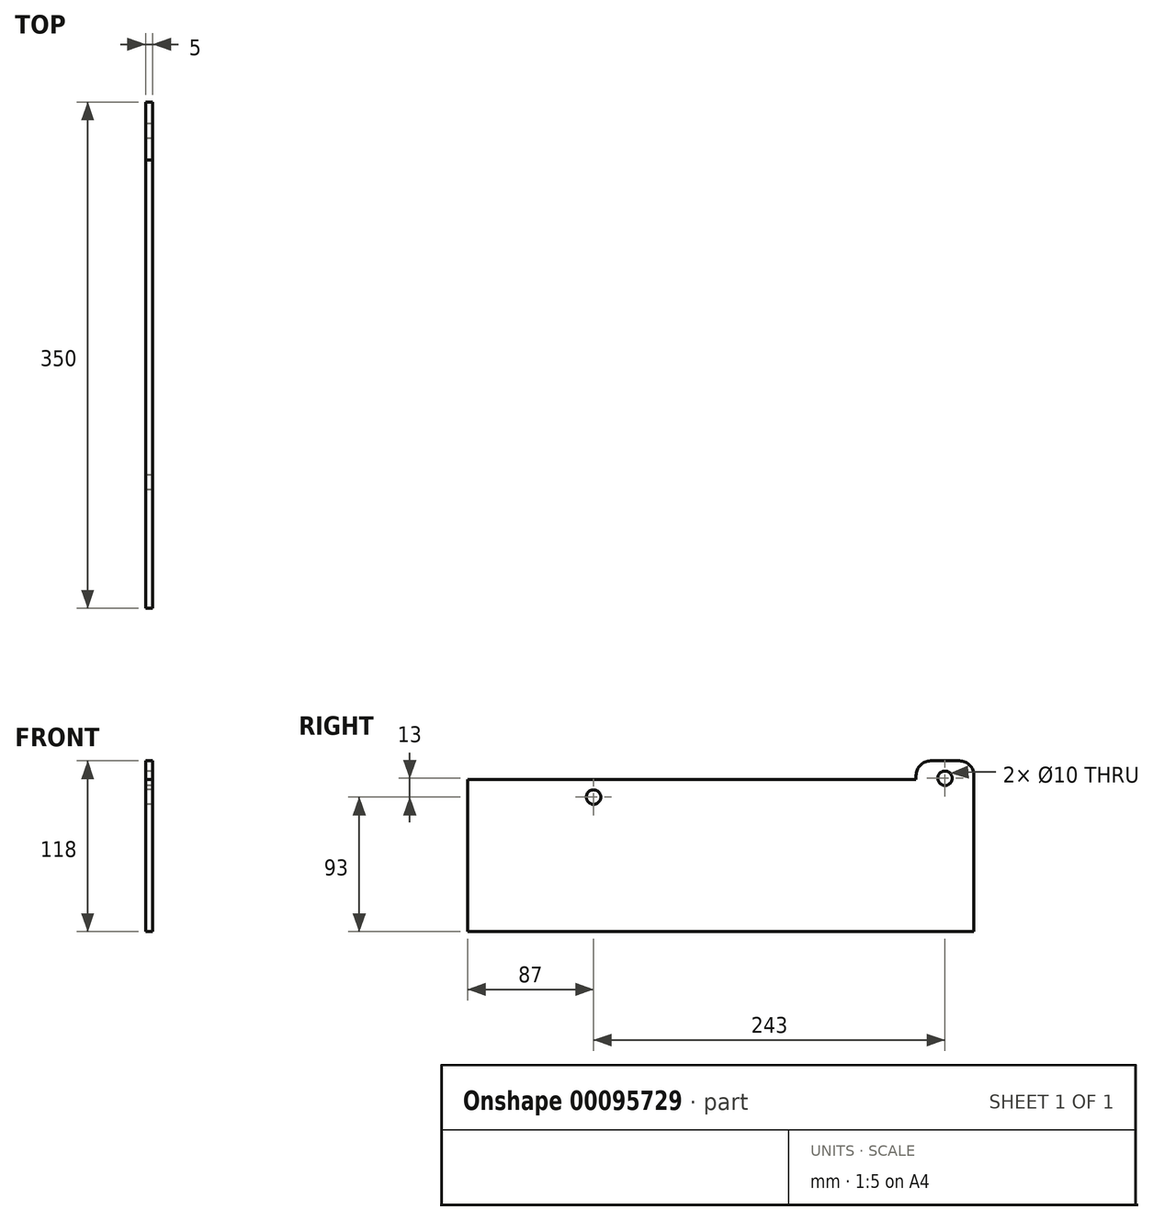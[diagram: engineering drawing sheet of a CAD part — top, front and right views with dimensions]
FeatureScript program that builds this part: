
annotation { "Feature Type Name" : "Feature", "Feature Type Description" : "" }
export const myFeature = defineFeature(function(context is Context, id is Id, definition is map)
    precondition{}
    {
        {
            var Q0;
            Q0=qCreatedBy(makeId("Right.planeOp"),FACE);
            var sketch = newSketch(context, id + "F0", { "sketchPlane" : qUnion([Q0])});
            skLineSegment(sketch, "E0", {"start": v(-330, -1) * mm, "end": v(-20, -1) * mm});
            skLineSegment(sketch, "E1", {"start": v(-20, -1) * mm, "end": v(-20, 2) * mm});
            skLineSegment(sketch, "E2", {"start": v(-10, 12) * mm, "end": v(10, 12) * mm});
            skLineSegment(sketch, "E3", {"start": v(20, 2) * mm, "end": v(20, -106) * mm});
            skLineSegment(sketch, "E4", {"start": v(20, -106) * mm, "end": v(-330, -106) * mm});
            skLineSegment(sketch, "E5", {"start": v(-330, -106) * mm, "end": v(-330, -1) * mm});
            skCircle(sketch, "E6", {"center": v(0, 0) * mm, "radius": 5 * mm});
            skCircle(sketch, "E7", {"center": v(-243, -13) * mm, "radius": 5 * mm});
            skPoint(sketch, "E8.visualSharp", {"position": v(-20, 12) * mm});
            skArc(sketch, "E8.filletArc", {"start": v(-10, 12) * mm, "mid": v(-17.07, 9.07) * mm, "end": v(-20, 2) * mm});
            skPoint(sketch, "E9.visualSharp", {"position": v(20, 12) * mm});
            skArc(sketch, "E9.filletArc", {"start": v(20, 2) * mm, "mid": v(17.07, 9.07) * mm, "end": v(10, 12) * mm});
            skSolve(sketch);
        }
        {
            var Q0;
            Q0=makeQuery(id+"F0.imprint","IMPRINT",FACE,{"disambiguationData":[TD([[makeQuery(id+"F0.imprint","IMPRINT",EDGE,{"derivedFrom":sQuery(id+"F0.wireOp",EDGE,"E0")}),-1.0]])]});
            var Q1;
            Q1 = qSketchRegion(id + "F0", true);
            extrude(context, id + "F1", {"entities" : qUnion([Q0, Q1]), "depth" : 5 * mm});
        }
    });
